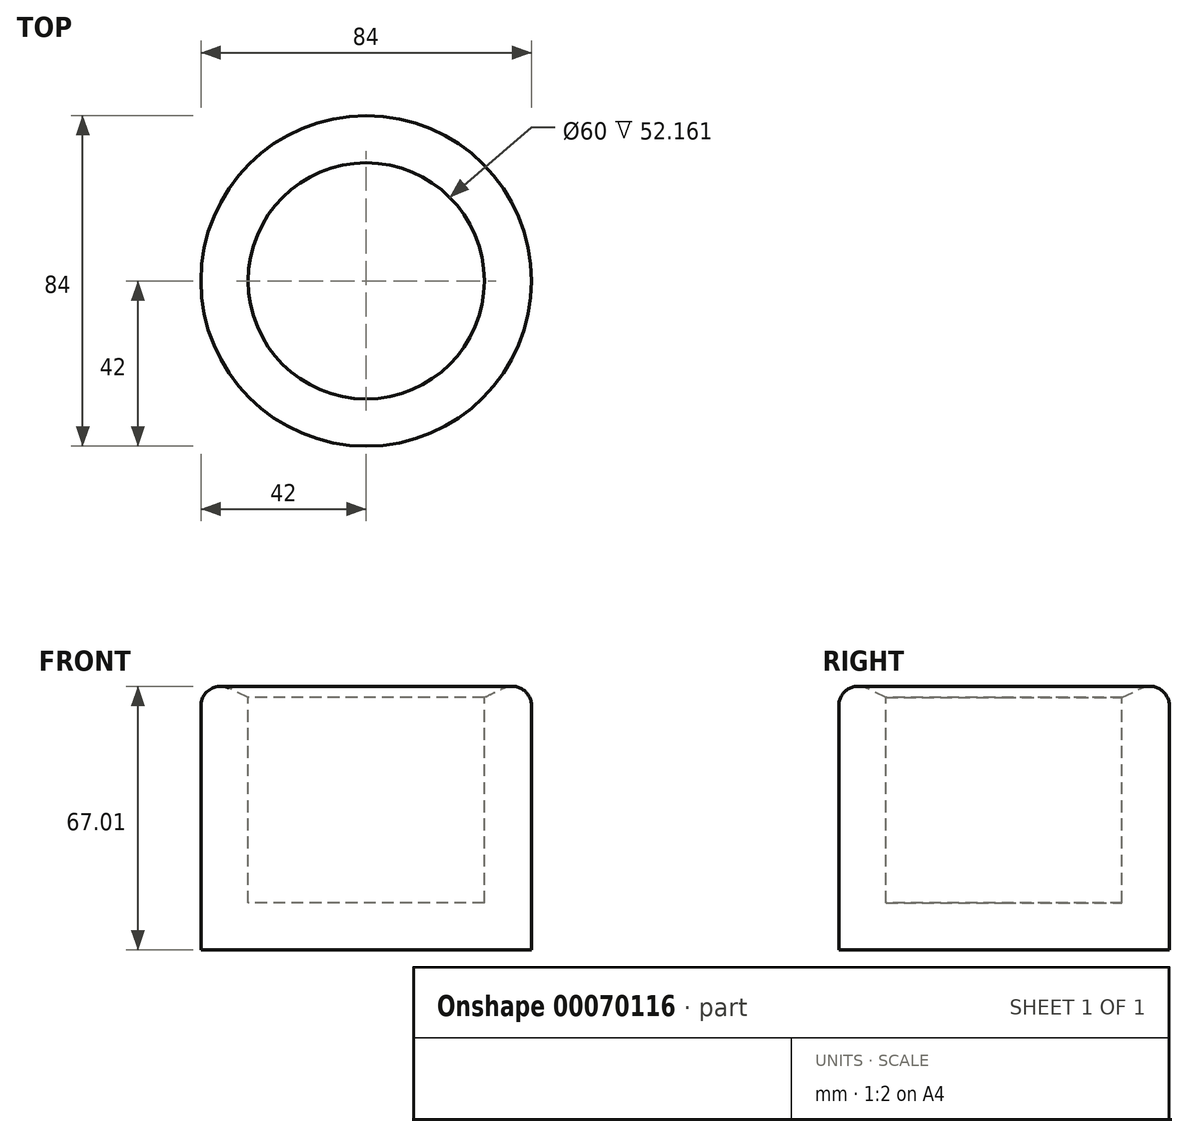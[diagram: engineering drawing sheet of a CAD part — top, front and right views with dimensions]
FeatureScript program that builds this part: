
annotation { "Feature Type Name" : "Feature", "Feature Type Description" : "" }
export const myFeature = defineFeature(function(context is Context, id is Id, definition is map)
    precondition{}
    {
        {
            var Q0;
            Q0=qCreatedBy(makeId("Front.planeOp"),FACE);
            var sketch = newSketch(context, id + "F0", { "sketchPlane" : qUnion([Q0])});
            skLineSegment(sketch, "E0", {"start": v(0, 0) * mm, "end": v(-42, 0) * mm});
            skLineSegment(sketch, "E1", {"start": v(-42, 0) * mm, "end": v(-42, 70) * mm});
            skLineSegment(sketch, "E2", {"start": v(-42, 70) * mm, "end": v(-30, 64.16) * mm});
            skLineSegment(sketch, "E3", {"start": v(-30, 64.16) * mm, "end": v(-30, 12) * mm});
            skLineSegment(sketch, "E4", {"start": v(-30, 12) * mm, "end": v(0, 12) * mm});
            skLineSegment(sketch, "E5", {"start": v(0, 12) * mm, "end": v(0, 0) * mm});
            skSolve(sketch);
        }
        {
            var Q0;
            Q0=makeQuery(id+"F0.imprint","IMPRINT",FACE,{"disambiguationData":[TD([[makeQuery(id+"F0.imprint","IMPRINT",EDGE,{"derivedFrom":sQuery(id+"F0.wireOp",EDGE,"E0")}),-1.0]])]});
            var Q1;
            Q1=sQuery(id+"F0.wireOp",EDGE,"E5");
            revolve(context, id + "F1", {"entities" : qUnion([Q0]), "axis" : qUnion([Q1]), "revolveType" : RevolveType.FULL});
        }
        {
            var Q0;
            Q0=makeQuery(id+"F1.opRevolve","SWEPT_EDGE",EDGE,{"disambiguationData":[OSD([sQuery(id+"F0.wireOp",EDGE,"E1"),sQuery(id+"F0.wireOp",EDGE,"E2")])]});
            fillet(context, id + "F2", {"entities" : qUnion([Q0]), "radius" : 5 * mm, "tangentPropagation" : true, "allowEdgeOverflow" : false});
        }
    });
